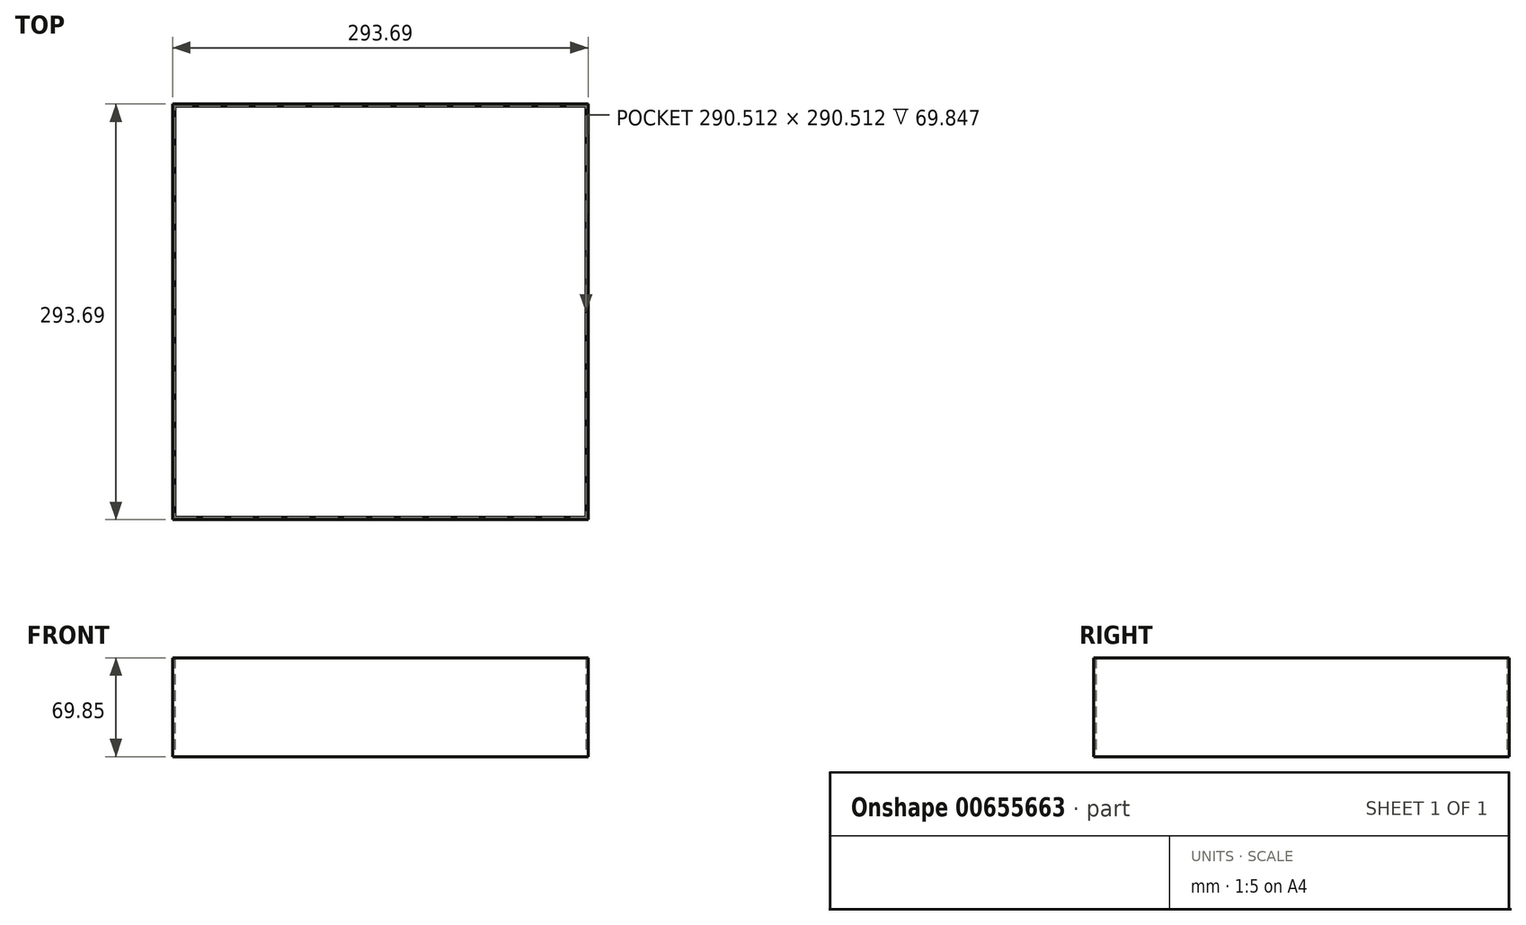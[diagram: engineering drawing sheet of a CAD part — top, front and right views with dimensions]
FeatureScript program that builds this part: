
annotation { "Feature Type Name" : "Feature", "Feature Type Description" : "" }
export const myFeature = defineFeature(function(context is Context, id is Id, definition is map)
    precondition{}
    {
        {
            var Q0;
            Q0=qCreatedBy(makeId("Top.planeOp"),FACE);
            var sketch = newSketch(context, id + "F0", { "sketchPlane" : qUnion([Q0])});
            skLineSegment(sketch, "E0.bottom", {"start": v(0, 0) * mm, "end": v(290.51, 0) * mm});
            skLineSegment(sketch, "E0.top", {"start": v(0, 290.51) * mm, "end": v(290.51, 290.51) * mm});
            skLineSegment(sketch, "E0.left", {"start": v(0, 0) * mm, "end": v(0, 290.51) * mm});
            skLineSegment(sketch, "E0.right", {"start": v(290.51, 0) * mm, "end": v(290.51, 290.51) * mm});
            skSolve(sketch);
        }
        {
            var Q0;
            Q0 = qSketchRegion(id + "F0", true);
            extrude(context, id + "F1", {"entities" : qUnion([Q0]), "depth" : 1 / 406.4 * mm, "offsetDistance" : 25.4 * mm});
        }
        {
            var Q0;
            Q0=makeQuery(id+"F1.opExtrude","CAP_FACE",FACE,{"disambiguationData":[OSD([sQuery(id+"F0.wireOp",EDGE,"E0.bottom"),sQuery(id+"F0.wireOp",EDGE,"E0.top"),sQuery(id+"F0.wireOp",EDGE,"E0.left"),sQuery(id+"F0.wireOp",EDGE,"E0.right")])],"isStart":true});
            var sketch = newSketch(context, id + "F2", { "sketchPlane" : qUnion([Q0])});
            skLineSegment(sketch, "E1.0", {"start": v(292.1, 1.59) * mm, "end": v(292.1, -292.1) * mm});
            skLineSegment(sketch, "E1.1", {"start": v(-1.59, 1.59) * mm, "end": v(292.1, 1.59) * mm});
            skLineSegment(sketch, "E1.2", {"start": v(-1.59, 1.59) * mm, "end": v(-1.59, -292.1) * mm});
            skLineSegment(sketch, "E1.3", {"start": v(-1.59, -292.1) * mm, "end": v(292.1, -292.1) * mm});
            skSolve(sketch);
        }
        {
            var Q0;
            Q0=makeQuery(id+"F2.imprint","IMPRINT",FACE,{"disambiguationData":[TD([[makeQuery(id+"F2.imprint","IMPRINT",EDGE,{"derivedFrom":sQuery(id+"F2.wireOp",EDGE,"E1.0")}),-1.0]])]});
            extrude(context, id + "F3", {"entities" : qUnion([Q0]), "operationType" : NewBodyOperationType.ADD, "oppositeDirection" : true, "depth" : 69.85 * mm, "offsetDistance" : 25.4 * mm});
        }
    });
